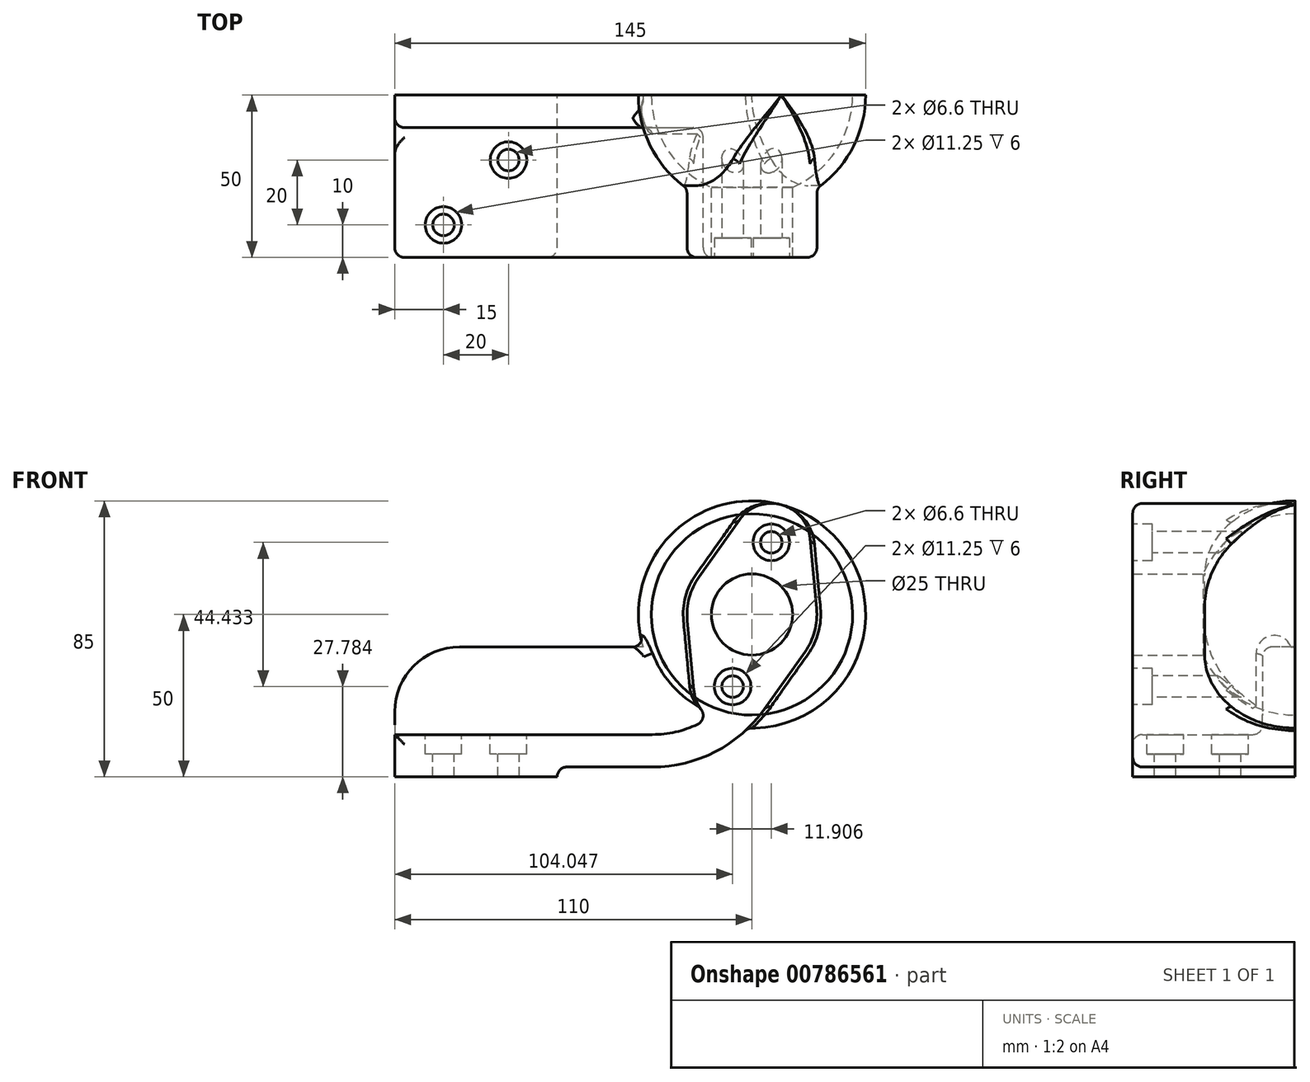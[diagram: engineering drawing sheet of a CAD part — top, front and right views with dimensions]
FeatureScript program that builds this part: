
annotation { "Feature Type Name" : "Feature", "Feature Type Description" : "" }
export const myFeature = defineFeature(function(context is Context, id is Id, definition is map)
    precondition{}
    {
        {
            var Q0;
            Q0=qCreatedBy(makeId("Front.planeOp"),FACE);
            var sketch = newSketch(context, id + "F0", { "sketchPlane" : qUnion([Q0])});
            skCircle(sketch, "E0", {"center": v(110, 50) * mm, "radius": 35 * mm});
            skCircle(sketch, "E1", {"center": v(110, 50) * mm, "radius": 12.5 * mm});
            skLineSegment(sketch, "E2", {"start": v(100.94, 16.2) * mm, "end": v(119.06, 83.8) * mm, "construction": true});
            skArc(sketch, "E3", {"start": v(108.97, 62.46) * mm, "mid": v(112.85, 60.63) * mm, "end": v(117.12, 60.27) * mm, "construction": true});
            skArc(sketch, "E4", {"start": v(92.1, 26.66) * mm, "mid": v(100.94, 16.2) * mm, "end": v(113.83, 20.84) * mm});
            skArc(sketch, "E5", {"start": v(93.69, 61.57) * mm, "mid": v(90.68, 55.18) * mm, "end": v(90.09, 48.13) * mm});
            skLineSegment(sketch, "E6", {"start": v(0, 0) * mm, "end": v(50, 0) * mm});
            skLineSegment(sketch, "E7", {"start": v(50, 0) * mm, "end": v(50, 3) * mm});
            skLineSegment(sketch, "E8", {"start": v(50, 3) * mm, "end": v(79.3, 3) * mm});
            skLineSegment(sketch, "E9", {"start": v(0, 0) * mm, "end": v(0, 40) * mm});
            skLineSegment(sketch, "E10", {"start": v(0, 40) * mm, "end": v(76.46, 40) * mm});
            skLineSegment(sketch, "E11", {"start": v(129.91, 51.87) * mm, "end": v(127.9, 73.34) * mm});
            skLineSegment(sketch, "E12", {"start": v(93.69, 61.57) * mm, "end": v(106.17, 79.16) * mm});
            skLineSegment(sketch, "E13", {"start": v(90.09, 48.13) * mm, "end": v(92.1, 26.66) * mm});
            skLineSegment(sketch, "E14", {"start": v(126.31, 38.43) * mm, "end": v(113.83, 20.84) * mm});
            skArc(sketch, "E15.trimOffspring", {"start": v(127.9, 73.34) * mm, "mid": v(119.06, 83.8) * mm, "end": v(106.17, 79.16) * mm});
            skArc(sketch, "E16.trimOffspring", {"start": v(111.03, 37.54) * mm, "mid": v(107.15, 39.37) * mm, "end": v(102.88, 39.73) * mm, "construction": true});
            skArc(sketch, "E17.trimOffspring", {"start": v(126.31, 38.43) * mm, "mid": v(129.32, 44.82) * mm, "end": v(129.91, 51.87) * mm});
            skArc(sketch, "E18", {"start": v(79.3, 3) * mm, "mid": v(98.74, 7.72) * mm, "end": v(113.83, 20.84) * mm});
            skArc(sketch, "E19.0", {"start": v(79.3, 13) * mm, "mid": v(88.45, 14.32) * mm, "end": v(96.86, 18.18) * mm});
            skLineSegment(sketch, "E20", {"start": v(0, 13) * mm, "end": v(79.3, 13) * mm});
            skSolve(sketch);
        }
        {
            var Q0;
            Q0=makeQuery(id+"F0.imprint","IMPRINT",FACE,{"disambiguationData":[TD([[makeQuery(id+"F0.imprint","IMPRINT",EDGE,{"derivedFrom":sQuery(id+"F0.wireOp",EDGE,"E5")}),-1.0]])]});
            var sketch = newSketch(context, id + "F1", { "sketchPlane" : qUnion([Q0])});
            skArc(sketch, "E21.0", {"start": v(109.02, 84.99) * mm, "mid": v(75.01, 49.02) * mm, "end": v(110.98, 15.01) * mm});
            skLineSegment(sketch, "E22", {"start": v(109.02, 84.99) * mm, "end": v(110.98, 15.01) * mm});
            skSolve(sketch);
        }
        {
            var Q0;
            Q0=qSketchRegion(id+"F1",true);
            var Q1;
            Q1=sQuery(id+"F1.wireOp",EDGE,"E22");
            revolve(context, id + "F2", {"surfaceOperationType" : NewSurfaceOperationType.NEW, "entities" : qUnion([Q0]), "axis" : qUnion([Q1]), "revolveType" : RevolveType.ONE_DIRECTION, "oppositeDirection" : true, "angle" : 180 * degree});
        }
        {
            var Q0;
            {var subQ0=sQuery(id+"F0.wireOp",EDGE,"E19.0");var subQ1=sQuery(id+"F0.wireOp",EDGE,"E0");var subQ2=makeQuery(id+"F0.imprint","INTERSECT",VERTEX,{"derivedFrom":[subQ1,subQ0]});Q0=makeQuery(id+"F0.imprint","IMPRINT",FACE,{"disambiguationData":[TD([[makeQuery(id+"F0.imprint","IMPRINT",EDGE,{"disambiguationData":[TD([[subQ2,-1.0]])],"derivedFrom":subQ1}),1.0]])]});}
            var Q1;
            {var subQ0=sQuery(id+"F0.wireOp",EDGE,"E18");var subQ1=sQuery(id+"F0.wireOp",EDGE,"E0");var subQ2=makeQuery(id+"F0.imprint","INTERSECT",VERTEX,{"derivedFrom":[subQ1,subQ0]});Q1=makeQuery(id+"F0.imprint","IMPRINT",FACE,{"disambiguationData":[TD([[makeQuery(id+"F0.imprint","IMPRINT",EDGE,{"disambiguationData":[TD([[subQ2,1.0]])],"derivedFrom":subQ1}),1.0]])]});}
            var Q2;
            {var subQ0=sQuery(id+"F0.wireOp",EDGE,"E6");Q2=makeQuery(id+"F0.imprint","IMPRINT",FACE,{"disambiguationData":[TD([[makeQuery(id+"F0.imprint","IMPRINT",EDGE,{"derivedFrom":subQ0}),1.0]])]});}
            var Q3;
            Q3=makeQuery(id+"F0.imprint","IMPRINT",FACE,{"disambiguationData":[TD([[makeQuery(id+"F0.imprint","IMPRINT",EDGE,{"derivedFrom":sQuery(id+"F0.wireOp",EDGE,"E1")}),-1.0]])]});
            var Q4;
            Q4=makeQuery(id+"F0.imprint","IMPRINT",FACE,{"disambiguationData":[TD([[makeQuery(id+"F0.imprint","IMPRINT",EDGE,{"derivedFrom":sQuery(id+"F0.wireOp",EDGE,"E1")}),1.0]])]});
            extrude(context, id + "F3", {"entities" : qUnion([Q0, Q1, Q2, Q3, Q4]), "operationType" : NewBodyOperationType.ADD, "depth" : 50 * mm, "offsetDistance" : 25 * mm});
        }
        {
            var Q0;
            Q0=makeQuery(id+"F3.opExtrude","SWEPT_FACE",FACE,{"disambiguationData":[OSD([sQuery(id+"F0.wireOp",EDGE,"E9")])]});
            var sketch = newSketch(context, id + "F4", { "sketchPlane" : qUnion([Q0])});
            skLineSegment(sketch, "E23.bottom", {"start": v(0, 13) * mm, "end": v(10, 13) * mm});
            skLineSegment(sketch, "E23.top", {"start": v(0, 40) * mm, "end": v(10, 40) * mm});
            skLineSegment(sketch, "E23.left", {"start": v(0, 13) * mm, "end": v(0, 40) * mm});
            skLineSegment(sketch, "E23.right", {"start": v(10, 13) * mm, "end": v(10, 40) * mm});
            skSolve(sketch);
        }
        {
            var Q0;
            Q0=makeQuery(id+"F4.imprint","IMPRINT",FACE,{"disambiguationData":[TD([[makeQuery(id+"F4.imprint","IMPRINT",EDGE,{"derivedFrom":sQuery(id+"F4.wireOp",EDGE,"E23.bottom")}),-1.0]])]});
            extrude(context, id + "F5", {"entities" : qUnion([Q0]), "operationType" : NewBodyOperationType.ADD, "endBound" : BoundingType.UP_TO_NEXT, "oppositeDirection" : true, "depth" : 37.2 * mm, "offsetDistance" : 25 * mm});
        }
        {
            var Q0;
            Q0=makeQuery(id+"F5.opExtrude","CAP_EDGE",EDGE,{"disambiguationData":[OSD([sQuery(id+"F4.wireOp",EDGE,"E23.top")])],"isStart":true});
            fillet(context, id + "F6", {"entities" : qUnion([Q0]), "radius" : 20 * mm, "tangentPropagation" : true, "allowEdgeOverflow" : false});
        }
        {
            var Q0;
            {var subQ0=sQuery(id+"F0.wireOp",EDGE,"E20");Q0=makeQuery(id+"FL2OrtGu8nAbXdU_1.boolean.opBoolean","MERGE",FACE,{"derivedFrom":[makeQuery(id+"F3.opExtrude","SWEPT_FACE",FACE,{"disambiguationData":[OSD([subQ0])]}),makeQuery(id+"FL2OrtGu8nAbXdU_1.opExtrude","SWEPT_FACE",FACE,{"disambiguationData":[OSD([sQuery(id+"F0.wireOp",EDGE,"E9"),subQ0])]})]});}
            var sketch = newSketch(context, id + "F7", { "sketchPlane" : qUnion([Q0])});
            skPoint(sketch, "E24", {"position": v(15, -40) * mm});
            skPoint(sketch, "E25", {"position": v(35, -20) * mm});
            skSolve(sketch);
        }
        {
            var Q0;
            Q0=makeQuery(id+"F3.opExtrude","CAP_FACE",FACE,{"disambiguationData":[OSD([sQuery(id+"F0.wireOp",EDGE,"E1"),sQuery(id+"F0.wireOp",EDGE,"E4"),sQuery(id+"F0.wireOp",EDGE,"E5"),sQuery(id+"F0.wireOp",EDGE,"E6"),sQuery(id+"F0.wireOp",EDGE,"E7"),sQuery(id+"F0.wireOp",EDGE,"E8"),sQuery(id+"F0.wireOp",EDGE,"E9"),sQuery(id+"F0.wireOp",EDGE,"E11"),sQuery(id+"F0.wireOp",EDGE,"E12"),sQuery(id+"F0.wireOp",EDGE,"E13"),sQuery(id+"F0.wireOp",EDGE,"E14"),sQuery(id+"F0.wireOp",EDGE,"E15.trimOffspring"),sQuery(id+"F0.wireOp",EDGE,"E17.trimOffspring"),sQuery(id+"F0.wireOp",EDGE,"E18"),sQuery(id+"F0.wireOp",EDGE,"E19.0"),sQuery(id+"F0.wireOp",EDGE,"E20")])],"isStart":false});
            var sketch = newSketch(context, id + "F8", { "sketchPlane" : qUnion([Q0])});
            skCircle(sketch, "E26", {"center": v(110, 50) * mm, "radius": 23 * mm, "construction": true});
            skLineSegment(sketch, "E27", {"start": v(104.05, 27.78) * mm, "end": v(115.95, 72.22) * mm, "construction": true});
            skSolve(sketch);
        }
        {
            var Q0;
            Q0=sQuery(id+"F7.wireOp",VERTEX,"E25");
            var Q1;
            Q1=sQuery(id+"F7.wireOp",VERTEX,"E24");
            var Q2;
            Q2=sQuery(id+"F8.wireOp",VERTEX,"E27.end");
            var Q3;
            Q3=sQuery(id+"F8.wireOp",VERTEX,"E27.start");
            var Q4;
            Q4=makeQuery(id+"F2.opRevolve","SWEPT_BODY",BODY,{"disambiguationData":[OSD([sQuery(id+"F1.wireOp",EDGE,"E21.0"),sQuery(id+"F1.wireOp",EDGE,"E22")])]});
            hole(context, id + "F9", {"style" : HoleStyle.C_BORE, "endStyle" : HoleEndStyle.THROUGH, "standardTappedOrClearance" : lookupTablePath({ "standard" : "ISO", "fit" : "Normal", "size" : "M6", "type" : "Clearance" }), "standardBlindInLast" : lookupTablePath({ "fit" : "Standard", "standard" : "ISO", "size" : "M6", "type" : "Clearance" }), "holeDiameter" : 6.6 * mm, "cBoreDiameter" : 11.25 * mm, "cBoreDepth" : 6 * mm, "majorDiameter" : 5 * mm, "isTappedThrough" : true, "tappedDepth" : 12 * mm, "tapClearance" : 3, "locations" : qUnion([Q0, Q1, Q2, Q3]), "scope" : qUnion([Q4])});
        }
        {
            var Q0;
            Q0=makeQuery(id+"F5.boolean.opBoolean","MERGE",FACE,{"derivedFrom":[makeQuery(id+"F3.boolean.opBoolean","MERGE",FACE,{"derivedFrom":[makeQuery(id+"F2.opRevolve","CAP_FACE",FACE,{"disambiguationData":[OSD([sQuery(id+"F1.wireOp",EDGE,"E21.0"),sQuery(id+"F1.wireOp",EDGE,"E22")])],"isStart":true}),makeQuery(id+"F3.opExtrude","CAP_FACE",FACE,{"disambiguationData":[OSD([sQuery(id+"F0.wireOp",EDGE,"E1"),sQuery(id+"F0.wireOp",EDGE,"E4"),sQuery(id+"F0.wireOp",EDGE,"E5"),sQuery(id+"F0.wireOp",EDGE,"E6"),sQuery(id+"F0.wireOp",EDGE,"E7"),sQuery(id+"F0.wireOp",EDGE,"E8"),sQuery(id+"F0.wireOp",EDGE,"E9"),sQuery(id+"F0.wireOp",EDGE,"E11"),sQuery(id+"F0.wireOp",EDGE,"E12"),sQuery(id+"F0.wireOp",EDGE,"E13"),sQuery(id+"F0.wireOp",EDGE,"E14"),sQuery(id+"F0.wireOp",EDGE,"E15.trimOffspring"),sQuery(id+"F0.wireOp",EDGE,"E17.trimOffspring"),sQuery(id+"F0.wireOp",EDGE,"E18"),sQuery(id+"F0.wireOp",EDGE,"E19.0"),sQuery(id+"F0.wireOp",EDGE,"E20")])],"isStart":true})]}),makeQuery(id+"F5.opExtrude","SWEPT_FACE",FACE,{"disambiguationData":[OSD([sQuery(id+"F4.wireOp",EDGE,"E23.left")])]})]});
            var sketch = newSketch(context, id + "F10", { "sketchPlane" : qUnion([Q0])});
            skArc(sketch, "E28.0", {"start": v(-121.95, 78.6) * mm, "mid": v(-138.6, 38.05) * mm, "end": v(-98.05, 21.4) * mm});
            skLineSegment(sketch, "E29", {"start": v(-98.05, 21.4) * mm, "end": v(-121.95, 78.6) * mm});
            skSolve(sketch);
        }
        {
            var Q0;
            Q0=qSketchRegion(id+"F10",true);
            var Q1;
            Q1=sQuery(id+"F10.wireOp",EDGE,"E29");
            revolve(context, id + "F11", {"operationType" : NewBodyOperationType.REMOVE, "surfaceOperationType" : NewSurfaceOperationType.NEW, "entities" : qUnion([Q0]), "axis" : qUnion([Q1]), "revolveType" : RevolveType.FULL, "oppositeDirection" : true});
        }
        {
            var Q0;
            Q0=makeQuery(id+"F0.imprint","IMPRINT",FACE,{"disambiguationData":[TD([[makeQuery(id+"F0.imprint","IMPRINT",EDGE,{"derivedFrom":sQuery(id+"F0.wireOp",EDGE,"E1")}),1.0]])]});
            extrude(context, id + "F12", {"entities" : qUnion([Q0]), "operationType" : NewBodyOperationType.REMOVE, "endBound" : BoundingType.THROUGH_ALL, "depth" : 106.3 * mm, "offsetDistance" : 25 * mm});
        }
        {
            var Q0;
            Q0=makeQuery(id+"F5.opExtrude","SWEPT_FACE",FACE,{"disambiguationData":[OSD([sQuery(id+"F4.wireOp",EDGE,"E23.right")])]});
            var Q1;
            Q1=makeQuery(id+"F3.opExtrude","CAP_EDGE",EDGE,{"disambiguationData":[OSD([sQuery(id+"F0.wireOp",EDGE,"E20")])],"isStart":false});
            var Q2;
            Q2=makeQuery(id+"F3.opExtrude","CAP_EDGE",EDGE,{"disambiguationData":[OSD([sQuery(id+"F0.wireOp",EDGE,"E9")])],"isStart":false});
            var Q3;
            Q3=makeQuery(id+"F3.opExtrude","SWEPT_EDGE",EDGE,{"disambiguationData":[OSD([sQuery(id+"F0.wireOp",EDGE,"E7"),sQuery(id+"F0.wireOp",EDGE,"E8")])]});
            var Q4;
            Q4=makeQuery(id+"F3.opExtrude","CAP_EDGE",EDGE,{"disambiguationData":[OSD([sQuery(id+"F0.wireOp",EDGE,"E8")])],"isStart":false});
            var Q5;
            Q5=makeQuery(id+"F3.opExtrude","SWEPT_EDGE",EDGE,{"disambiguationData":[OSD([sQuery(id+"F0.wireOp",EDGE,"E4"),sQuery(id+"F0.wireOp",EDGE,"E19.0")])]});
            var Q6;
            Q6=makeQuery(id+"F3.boolean.opBoolean","INTERSECT",EDGE,{"derivedFrom":[makeQuery(id+"F2.opRevolve","SWEPT_FACE",FACE,{"disambiguationData":[OSD([sQuery(id+"F1.wireOp",EDGE,"E21.0")])]}),makeQuery(id+"F3.opExtrude","SWEPT_FACE",FACE,{"disambiguationData":[OSD([sQuery(id+"F0.wireOp",EDGE,"E12")])]})]});
            var Q7;
            Q7=makeQuery(id+"F3.boolean.opBoolean","INTERSECT",EDGE,{"disambiguationData":[OD(0.0)],"derivedFrom":[makeQuery(id+"F2.opRevolve","SWEPT_FACE",FACE,{"disambiguationData":[OSD([sQuery(id+"F1.wireOp",EDGE,"E21.0")])]}),makeQuery(id+"F3.opExtrude","SWEPT_FACE",FACE,{"disambiguationData":[OSD([sQuery(id+"F0.wireOp",EDGE,"E15.trimOffspring")])]})]});
            fillet(context, id + "F13", {"entities" : qUnion([Q0, Q1, Q2, Q3, Q4, Q5, Q6, Q7]), "radius" : 3 * mm, "tangentPropagation" : true, "allowEdgeOverflow" : false});
        }
    });
